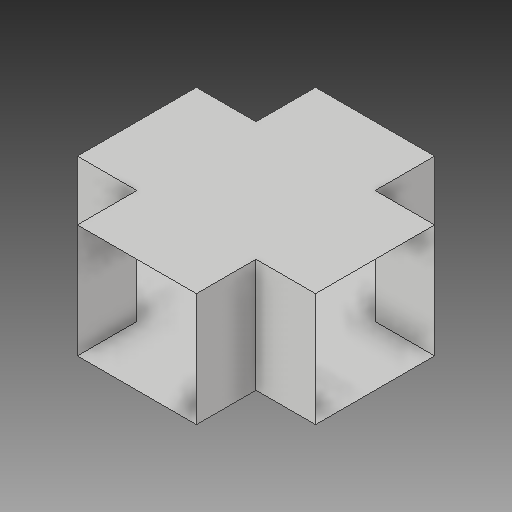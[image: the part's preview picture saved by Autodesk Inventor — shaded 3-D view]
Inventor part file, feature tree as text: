
AUTODESK INVENTOR PART (.ipt)
format: ipt  version: 2017 (Build 210142000, 142)  size: 113,664 bytes
history: native  units: in
note: dims shown in document units (in); Inventor stores cm internally (conversion verified against a paired STEP export)
features: extrude x1, pattern_circular x1, other x1, sketch x1
ambient origin geometry x8: Origin, YZ Plane, XZ Plane, XY Plane, X Axis, Y Axis, Z Axis, Center Point
bodies: Solid1 (feature_tree)
feature tree (4):
  extrude  "corridors"  Depth=6.6667in
  pattern_circular  "3 more corridors"  [2 undecoded]
  other  "removed ends"
  sketch  "Sketch1"  dims[d0=7.0in d1=6.6667in d2=7.0in d3=0.0in d4=1.5748in d5=360.0deg]
note: 2 required parameter values undecoded (feature->parameter linkage not recoverable at this tier; creation-order binding heuristic only, values carry confidence <= 0.55)
